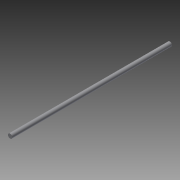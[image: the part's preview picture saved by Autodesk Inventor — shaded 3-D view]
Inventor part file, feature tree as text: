
AUTODESK INVENTOR PART (.ipt)
format: ipt  version: 2013 (Build 170138000, 138)  size: 64,000 bytes
history: native  units: in
note: dims shown in document units (in); Inventor stores cm internally (conversion verified against a paired STEP export)
features: extrude x1, sketch x1
ambient origin geometry x8: Origin, YZ Plane, XZ Plane, XY Plane, X Axis, Y Axis, Z Axis, Center Point
bodies: Solid1 (feature_tree)
feature tree (2):
  extrude  "Extrusion1"  Depth=14.0in TaperAngle=0.0deg
  sketch  "Sketch1"  dims[d0=0.375in d1=14.0in d2=0.0in]
